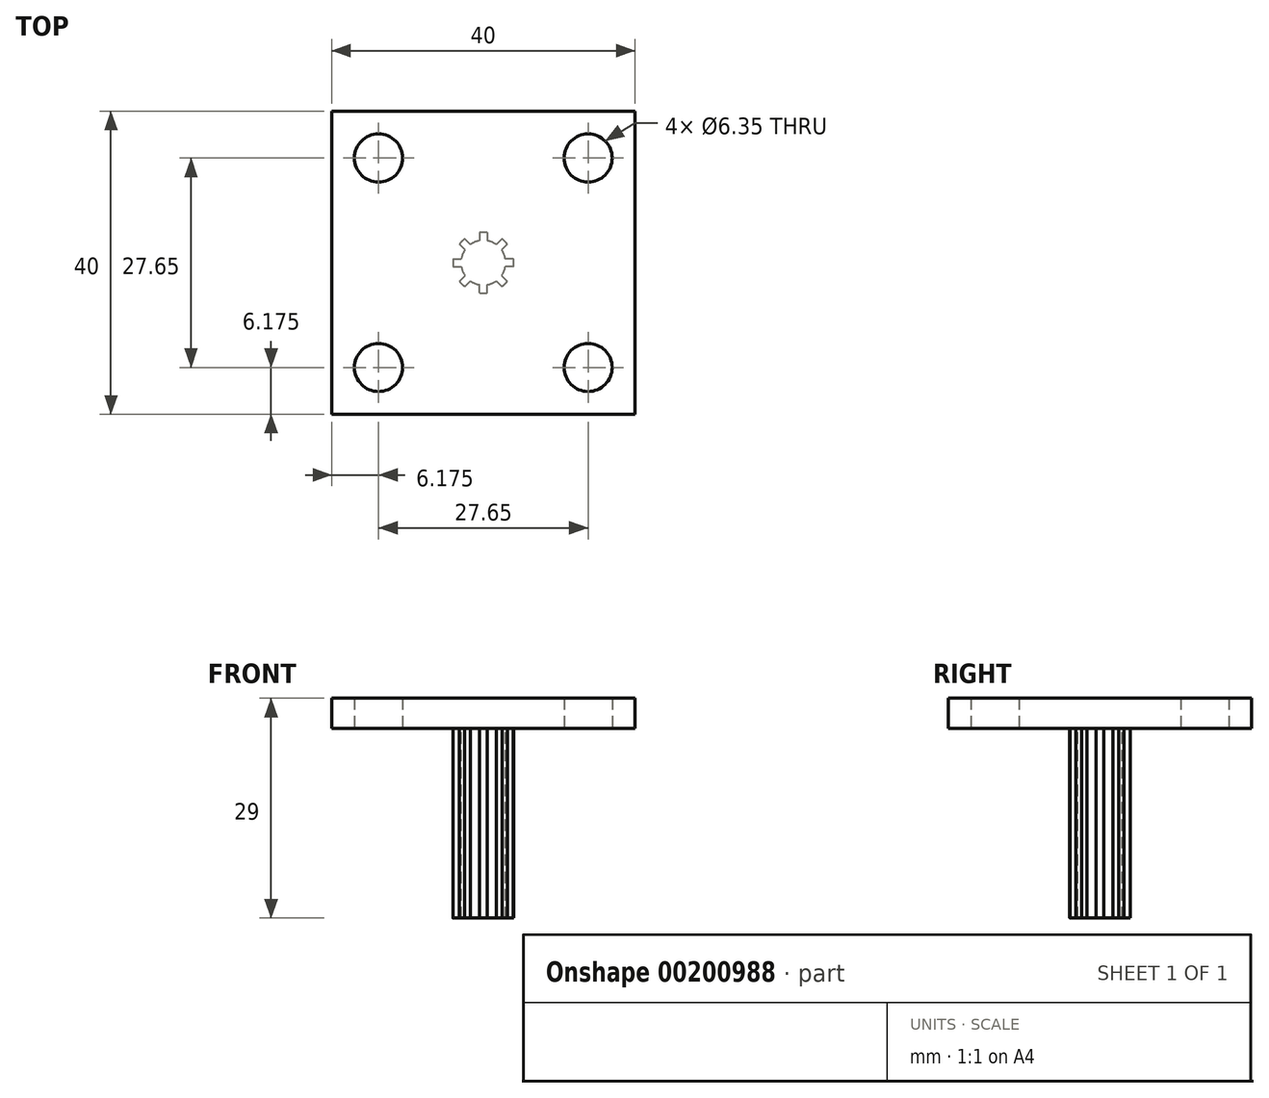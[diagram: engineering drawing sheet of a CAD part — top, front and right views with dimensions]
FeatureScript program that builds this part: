
annotation { "Feature Type Name" : "Feature", "Feature Type Description" : "" }
export const myFeature = defineFeature(function(context is Context, id is Id, definition is map)
    precondition{}
    {
        {
            var Q0;
            Q0=qCreatedBy(makeId("Top.planeOp"),FACE);
            var sketch = newSketch(context, id + "F0", { "sketchPlane" : qUnion([Q0])});
            skLineSegment(sketch, "E0.bottom", {"start": v(20, 20) * mm, "end": v(-20, 20) * mm});
            skLineSegment(sketch, "E0.top", {"start": v(20, -20) * mm, "end": v(-20, -20) * mm});
            skLineSegment(sketch, "E0.left", {"start": v(20, 20) * mm, "end": v(20, -20) * mm});
            skLineSegment(sketch, "E0.right", {"start": v(-20, 20) * mm, "end": v(-20, -20) * mm});
            skPoint(sketch, "E0.middle", {"position": v(0, 0) * mm});
            skCircle(sketch, "E1", {"center": v(-13.82, 13.82) * mm, "radius": 3.18 * mm});
            skLineSegment(sketch, "E2", {"start": v(0, 0) * mm, "end": v(0, 20) * mm, "construction": true});
            skLineSegment(sketch, "E3", {"start": v(0, 0) * mm, "end": v(20, 0) * mm, "construction": true});
            skCircle(sketch, "E4.1.0", {"center": v(-13.82, -13.82) * mm, "radius": 3.18 * mm});
            skCircle(sketch, "E4.2.0", {"center": v(13.82, -13.82) * mm, "radius": 3.18 * mm});
            skCircle(sketch, "E4.3.0", {"center": v(13.82, 13.82) * mm, "radius": 3.18 * mm});
            skSolve(sketch);
        }
        {
            var Q0;
            Q0 = qSketchRegion(id + "F0", true);
            extrude(context, id + "F1", {"entities" : qUnion([Q0]), "depth" : 4 * mm});
        }
        {
            var Q0;
            Q0=makeQuery(id+"F1.opExtrude","CAP_FACE",FACE,{"disambiguationData":[OSD([sQuery(id+"F0.wireOp",EDGE,"E0.bottom"),sQuery(id+"F0.wireOp",EDGE,"E0.top"),sQuery(id+"F0.wireOp",EDGE,"E0.left"),sQuery(id+"F0.wireOp",EDGE,"E0.right"),sQuery(id+"F0.wireOp",EDGE,"E1"),sQuery(id+"F0.wireOp",EDGE,"E4.1.0"),sQuery(id+"F0.wireOp",EDGE,"E4.2.0"),sQuery(id+"F0.wireOp",EDGE,"E4.3.0")])],"isStart":true});
            var sketch = newSketch(context, id + "F2", { "sketchPlane" : qUnion([Q0])});
            skCircle(sketch, "E5.0", {"center": v(0, 0) * mm, "radius": 2.95 * mm});
            skCircle(sketch, "E6", {"center": v(0, 0) * mm, "radius": 4 * mm});
            skLineSegment(sketch, "E7", {"start": v(0, 0) * mm, "end": v(0, 4) * mm, "construction": true});
            skLineSegment(sketch, "E8", {"start": v(-0.5, 3.97) * mm, "end": v(-0.5, 2.9) * mm});
            skLineSegment(sketch, "E9", {"start": v(0.5, 3.97) * mm, "end": v(0.5, 2.9) * mm});
            skLineSegment(sketch, "E10.1.0", {"start": v(-2.45, 3.16) * mm, "end": v(-1.7, 2.4) * mm});
            skLineSegment(sketch, "E10.1.1", {"start": v(-3.16, 2.45) * mm, "end": v(-2.4, 1.7) * mm});
            skLineSegment(sketch, "E10.2.0", {"start": v(-3.97, 0.5) * mm, "end": v(-2.9, 0.5) * mm});
            skLineSegment(sketch, "E10.2.1", {"start": v(-3.97, -0.5) * mm, "end": v(-2.9, -0.5) * mm});
            skLineSegment(sketch, "E10.3.0", {"start": v(-3.16, -2.45) * mm, "end": v(-2.4, -1.7) * mm});
            skLineSegment(sketch, "E10.3.1", {"start": v(-2.45, -3.16) * mm, "end": v(-1.7, -2.4) * mm});
            skLineSegment(sketch, "E10.4.0", {"start": v(-0.5, -3.97) * mm, "end": v(-0.5, -2.9) * mm});
            skLineSegment(sketch, "E10.4.1", {"start": v(0.5, -3.97) * mm, "end": v(0.5, -2.9) * mm});
            skLineSegment(sketch, "E10.5.0", {"start": v(2.45, -3.16) * mm, "end": v(1.7, -2.4) * mm});
            skLineSegment(sketch, "E10.5.1", {"start": v(3.16, -2.45) * mm, "end": v(2.4, -1.7) * mm});
            skLineSegment(sketch, "E10.6.0", {"start": v(3.97, -0.5) * mm, "end": v(2.9, -0.5) * mm});
            skLineSegment(sketch, "E10.6.1", {"start": v(3.97, 0.5) * mm, "end": v(2.9, 0.5) * mm});
            skLineSegment(sketch, "E10.7.0", {"start": v(3.16, 2.45) * mm, "end": v(2.4, 1.7) * mm});
            skLineSegment(sketch, "E10.7.1", {"start": v(2.45, 3.16) * mm, "end": v(1.7, 2.4) * mm});
            skSolve(sketch);
        }
        {
            var Q0;
            {var subQ0=sQuery(id+"F2.wireOp",EDGE,"E10.7.0");Q0=makeQuery(id+"F2.imprint","IMPRINT",FACE,{"disambiguationData":[TD([[makeQuery(id+"F2.imprint","IMPRINT",EDGE,{"derivedFrom":subQ0}),-1.0]])]});}
            var Q1;
            {var subQ0=sQuery(id+"F2.wireOp",EDGE,"E8");Q1=makeQuery(id+"F2.imprint","IMPRINT",FACE,{"disambiguationData":[TD([[makeQuery(id+"F2.imprint","IMPRINT",EDGE,{"derivedFrom":subQ0}),1.0]])]});}
            var Q2;
            {var subQ0=sQuery(id+"F2.wireOp",EDGE,"E10.1.0");Q2=makeQuery(id+"F2.imprint","IMPRINT",FACE,{"disambiguationData":[TD([[makeQuery(id+"F2.imprint","IMPRINT",EDGE,{"derivedFrom":subQ0}),-1.0]])]});}
            var Q3;
            {var subQ0=sQuery(id+"F2.wireOp",EDGE,"E10.2.0");Q3=makeQuery(id+"F2.imprint","IMPRINT",FACE,{"disambiguationData":[TD([[makeQuery(id+"F2.imprint","IMPRINT",EDGE,{"derivedFrom":subQ0}),-1.0]])]});}
            var Q4;
            {var subQ0=sQuery(id+"F2.wireOp",EDGE,"E10.3.0");Q4=makeQuery(id+"F2.imprint","IMPRINT",FACE,{"disambiguationData":[TD([[makeQuery(id+"F2.imprint","IMPRINT",EDGE,{"derivedFrom":subQ0}),-1.0]])]});}
            var Q5;
            {var subQ0=sQuery(id+"F2.wireOp",EDGE,"E10.4.0");Q5=makeQuery(id+"F2.imprint","IMPRINT",FACE,{"disambiguationData":[TD([[makeQuery(id+"F2.imprint","IMPRINT",EDGE,{"derivedFrom":subQ0}),-1.0]])]});}
            var Q6;
            {var subQ0=sQuery(id+"F2.wireOp",EDGE,"E10.5.0");Q6=makeQuery(id+"F2.imprint","IMPRINT",FACE,{"disambiguationData":[TD([[makeQuery(id+"F2.imprint","IMPRINT",EDGE,{"derivedFrom":subQ0}),-1.0]])]});}
            var Q7;
            {var subQ0=sQuery(id+"F2.wireOp",EDGE,"E10.6.0");Q7=makeQuery(id+"F2.imprint","IMPRINT",FACE,{"disambiguationData":[TD([[makeQuery(id+"F2.imprint","IMPRINT",EDGE,{"derivedFrom":subQ0}),-1.0]])]});}
            var Q8;
            {var subQ0=sQuery(id+"F2.wireOp",EDGE,"E5.0");var subQ9=makeQuery(id+"F2.imprint","INTERSECT",VERTEX,{"derivedFrom":[subQ0,sQuery(id+"F2.wireOp",EDGE,"E10.6.1")]});Q8=makeQuery(id+"F2.imprint","IMPRINT",FACE,{"disambiguationData":[TD([[makeQuery(id+"F2.imprint","IMPRINT",EDGE,{"disambiguationData":[TD([[subQ9,-1.0]])],"derivedFrom":subQ0}),1.0]])]});}
            extrude(context, id + "F3", {"entities" : qUnion([Q0, Q1, Q2, Q3, Q4, Q5, Q6, Q7, Q8]), "operationType" : NewBodyOperationType.ADD, "depth" : 25 * mm});
        }
    });
